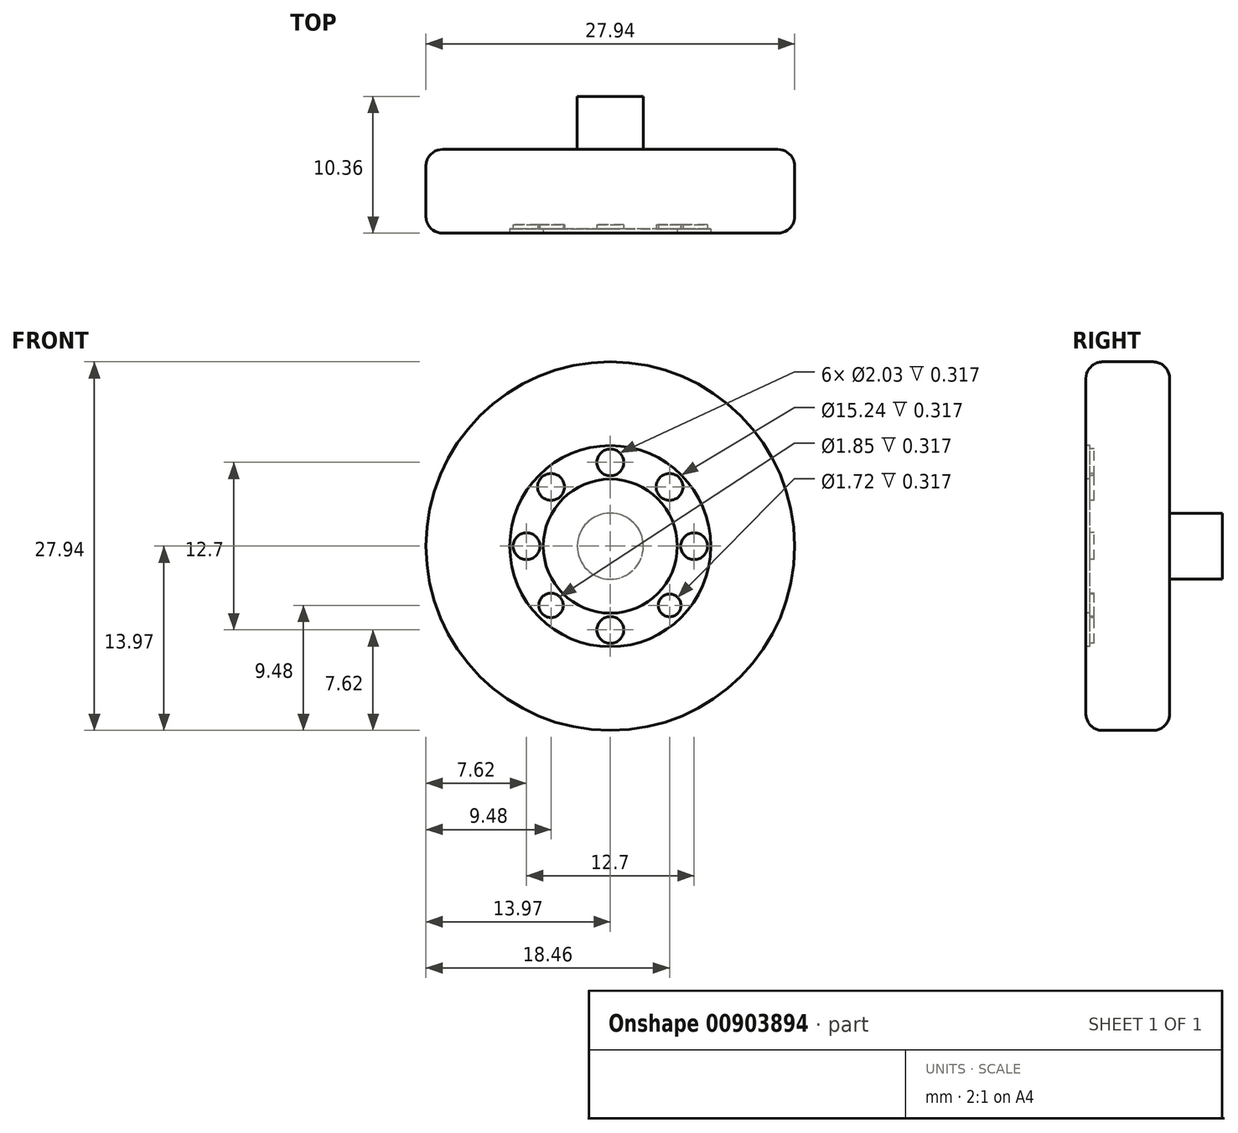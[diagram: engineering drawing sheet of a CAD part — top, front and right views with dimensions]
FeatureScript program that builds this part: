
annotation { "Feature Type Name" : "Feature", "Feature Type Description" : "" }
export const myFeature = defineFeature(function(context is Context, id is Id, definition is map)
    precondition{}
    {
        {
            var Q0;
            Q0=qCreatedBy(makeId("Front.planeOp"),FACE);
            var sketch = newSketch(context, id + "F0", { "sketchPlane" : qUnion([Q0])});
            skCircle(sketch, "E0", {"center": v(0, 0) * mm, "radius": 13.97 * mm});
            skSolve(sketch);
        }
        {
            var Q0;
            Q0 = qSketchRegion(id + "F0", true);
            extrude(context, id + "F1", {"entities" : qUnion([Q0]), "endBound" : BoundingType.SYMMETRIC, "depth" : 6.35 * mm, "offsetDistance" : 25.4 * mm});
        }
        {
            var Q0;
            Q0=makeQuery(id+"F1.opExtrude","CAP_EDGE",EDGE,{"disambiguationData":[OSD([sQuery(id+"F0.wireOp",EDGE,"E0")])],"isStart":false});
            var Q1;
            Q1=makeQuery(id+"F1.opExtrude","CAP_EDGE",EDGE,{"disambiguationData":[OSD([sQuery(id+"F0.wireOp",EDGE,"E0")])],"isStart":true});
            fillet(context, id + "F2", {"entities" : qUnion([Q0, Q1]), "radius" : 1.27 * mm, "tangentPropagation" : true, "allowEdgeOverflow" : false});
        }
        {
            var Q0;
            Q0=makeQuery(id+"F1.opExtrude","CAP_FACE",FACE,{"disambiguationData":[OSD([sQuery(id+"F0.wireOp",EDGE,"E0")])],"isStart":false});
            var sketch = newSketch(context, id + "F3", { "sketchPlane" : qUnion([Q0])});
            skCircle(sketch, "E1", {"center": v(0, 0) * mm, "radius": 10.16 * mm});
            skCircle(sketch, "E2", {"center": v(0, 0) * mm, "radius": 7.62 * mm});
            skCircle(sketch, "E3", {"center": v(0, 0) * mm, "radius": 5.08 * mm});
            skSolve(sketch);
        }
        {
            var Q0;
            Q0=makeQuery(id+"F3.imprint","IMPRINT",FACE,{"disambiguationData":[TD([[makeQuery(id+"F3.imprint","IMPRINT",EDGE,{"derivedFrom":sQuery(id+"F3.wireOp",EDGE,"E2")}),1.0]])]});
            extrude(context, id + "F4", {"entities" : qUnion([Q0]), "operationType" : NewBodyOperationType.REMOVE, "oppositeDirection" : true, "depth" : 0.32 * mm, "offsetDistance" : 25.4 * mm});
        }
        {
            var Q0;
            Q0=makeQuery(id+"F1.opExtrude","CAP_FACE",FACE,{"disambiguationData":[OSD([sQuery(id+"F0.wireOp",EDGE,"E0")])],"isStart":true});
            var sketch = newSketch(context, id + "F5", { "sketchPlane" : qUnion([Q0])});
            skCircle(sketch, "E4", {"center": v(0, 0) * mm, "radius": 2.5 * mm});
            skSolve(sketch);
        }
        {
            var Q0;
            Q0 = qSketchRegion(id + "F5", true);
            extrude(context, id + "F6", {"entities" : qUnion([Q0]), "operationType" : NewBodyOperationType.ADD, "depth" : 4 * mm, "offsetDistance" : 25.4 * mm});
        }
        {
            var Q0;
            Q0=makeQuery(id+"F4.boolean.opBoolean","COPY",FACE,{"derivedFrom":makeQuery(id+"F4.opExtrude","CAP_FACE",FACE,{"disambiguationData":[OSD([sQuery(id+"F3.wireOp",EDGE,"E2"),sQuery(id+"F3.wireOp",EDGE,"E3")])],"isStart":false})});
            var sketch = newSketch(context, id + "F7", { "sketchPlane" : qUnion([Q0])});
            skCircle(sketch, "E5", {"center": v(0, 6.35) * mm, "radius": 1.02 * mm});
            skCircle(sketch, "E6.MirrorC", {"center": v(0, -6.35) * mm, "radius": 1.02 * mm});
            skCircle(sketch, "E7", {"center": v(-6.35, 0) * mm, "radius": 1.02 * mm});
            skCircle(sketch, "E8.MirrorC", {"center": v(6.35, 0) * mm, "radius": 1.02 * mm});
            skLineSegment(sketch, "E9", {"start": v(0, 0) * mm, "end": v(-5.39, 5.39) * mm});
            skLineSegment(sketch, "E10", {"start": v(-5.39, 5.39) * mm, "end": v(5.39, -5.39) * mm});
            skLineSegment(sketch, "E11", {"start": v(0, 0) * mm, "end": v(-5.39, -5.39) * mm});
            skLineSegment(sketch, "E12", {"start": v(-5.39, -5.39) * mm, "end": v(3.6, 3.6) * mm});
            skCircle(sketch, "E13", {"center": v(-4.5, -4.5) * mm, "radius": 0.92 * mm});
            skLineSegment(sketch, "E14", {"start": v(3.6, 3.6) * mm, "end": v(5.39, 5.39) * mm});
            skCircle(sketch, "E15", {"center": v(4.5, 4.5) * mm, "radius": 1.02 * mm});
            skCircle(sketch, "E16", {"center": v(-4.5, 4.5) * mm, "radius": 1.02 * mm});
            skCircle(sketch, "E17", {"center": v(4.5, -4.5) * mm, "radius": 0.86 * mm});
            skSolve(sketch);
        }
        {
            var Q0;
            Q0 = qSketchRegion(id + "F7", true);
            extrude(context, id + "F8", {"entities" : qUnion([Q0]), "operationType" : NewBodyOperationType.REMOVE, "oppositeDirection" : true, "depth" : 0.32 * mm, "offsetDistance" : 25.4 * mm});
        }
    });
